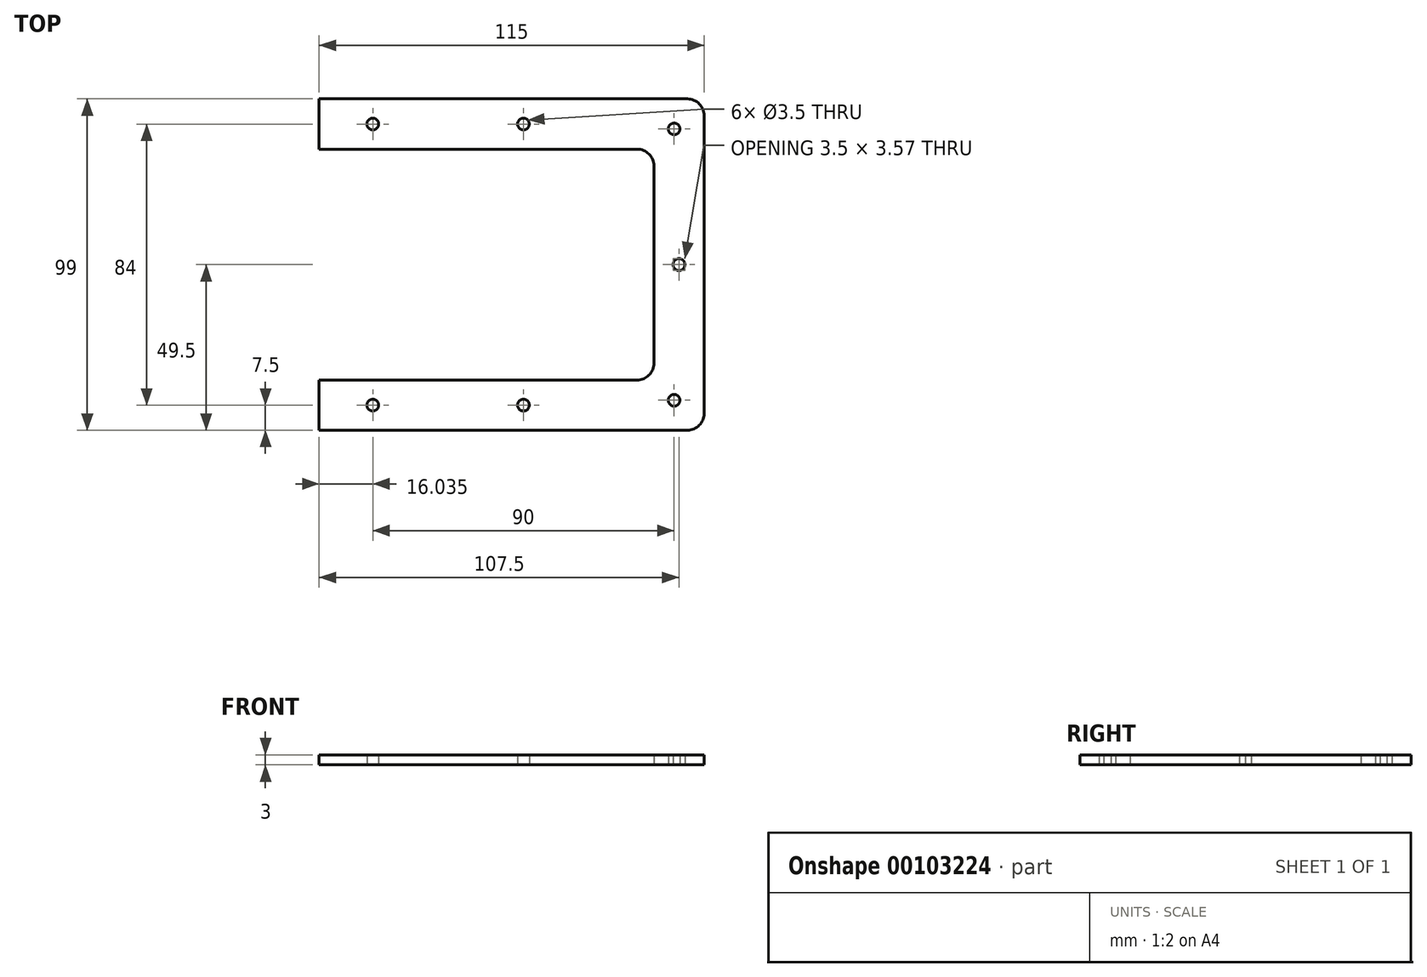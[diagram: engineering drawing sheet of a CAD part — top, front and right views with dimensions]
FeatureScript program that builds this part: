
annotation { "Feature Type Name" : "Feature", "Feature Type Description" : "" }
export const myFeature = defineFeature(function(context is Context, id is Id, definition is map)
    precondition{}
    {
        {
            var Q0;
            Q0=qCreatedBy(makeId("Top.planeOp"),FACE);
            var sketch = newSketch(context, id + "F0", { "sketchPlane" : qUnion([Q0])});
            skLineSegment(sketch, "E0.bottom", {"start": v(95, -34.5) * mm, "end": v(0, -34.5) * mm});
            skLineSegment(sketch, "E0.top", {"start": v(95, 34.5) * mm, "end": v(0, 34.5) * mm});
            skLineSegment(sketch, "E0.left", {"start": v(100, -29.5) * mm, "end": v(100, 29.5) * mm});
            skPoint(sketch, "E0.middle", {"position": v(0, 0) * mm});
            skLineSegment(sketch, "E1.1", {"start": v(110, -49.5) * mm, "end": v(0, -49.5) * mm});
            skLineSegment(sketch, "E1.2", {"start": v(115, -44.5) * mm, "end": v(115, 44.5) * mm});
            skLineSegment(sketch, "E1.3", {"start": v(110, 49.5) * mm, "end": v(0, 49.5) * mm});
            skPoint(sketch, "E2.visualSharp", {"position": v(115, -49.5) * mm});
            skArc(sketch, "E2.filletArc", {"start": v(110, -49.5) * mm, "mid": v(113.54, -48.04) * mm, "end": v(115, -44.5) * mm});
            skPoint(sketch, "E3.visualSharp", {"position": v(115, 49.5) * mm});
            skArc(sketch, "E3.filletArc", {"start": v(115, 44.5) * mm, "mid": v(113.54, 48.04) * mm, "end": v(110, 49.5) * mm});
            skPoint(sketch, "E4.visualSharp", {"position": v(100, 34.5) * mm});
            skArc(sketch, "E4.filletArc", {"start": v(100, 29.5) * mm, "mid": v(98.54, 33.04) * mm, "end": v(95, 34.5) * mm});
            skPoint(sketch, "E5.visualSharp", {"position": v(100, -34.5) * mm});
            skArc(sketch, "E5.filletArc", {"start": v(95, -34.5) * mm, "mid": v(98.54, -33.04) * mm, "end": v(100, -29.5) * mm});
            skLineSegment(sketch, "E6", {"start": v(0, 49.5) * mm, "end": v(0, 34.5) * mm, "construction": true});
            skLineSegment(sketch, "E7", {"start": v(0, 34.5) * mm, "end": v(0, 42) * mm, "construction": true});
            skLineSegment(sketch, "E8", {"start": v(0, 42) * mm, "end": v(102.5, 42) * mm, "construction": true});
            skLineSegment(sketch, "E9", {"start": v(100, 0) * mm, "end": v(115, 0) * mm, "construction": true});
            skLineSegment(sketch, "E10", {"start": v(107.5, 0) * mm, "end": v(107.5, 37) * mm, "construction": true});
            skArc(sketch, "E11.filletArc", {"start": v(107.5, 37) * mm, "mid": v(106.04, 40.54) * mm, "end": v(102.5, 42) * mm, "construction": true});
            skLineSegment(sketch, "E12", {"start": v(98.54, 33.04) * mm, "end": v(113.54, 48.04) * mm, "construction": true});
            skPoint(sketch, "E13", {"position": v(106.04, 40.54) * mm});
            skPoint(sketch, "E14", {"position": v(107.5, 0.04) * mm});
            skPoint(sketch, "E15", {"position": v(61.04, 42) * mm});
            skPoint(sketch, "E16", {"position": v(16.04, 42) * mm});
            skPoint(sketch, "E17.MirrorP", {"position": v(107.5, -0.04) * mm});
            skPoint(sketch, "E18.MirrorP", {"position": v(106.04, -40.54) * mm});
            skPoint(sketch, "E19.MirrorP", {"position": v(61.04, -42) * mm});
            skPoint(sketch, "E20.MirrorP", {"position": v(16.04, -42) * mm});
            skLineSegment(sketch, "E21", {"start": v(0, 49.5) * mm, "end": v(0, 34.5) * mm});
            skLineSegment(sketch, "E22", {"start": v(0, -34.5) * mm, "end": v(0, -49.5) * mm});
            skSolve(sketch);
        }
        {
            var Q0;
            Q0=makeQuery(id+"F0.imprint","IMPRINT",FACE,{"disambiguationData":[TD([[makeQuery(id+"F0.imprint","IMPRINT",EDGE,{"derivedFrom":sQuery(id+"F0.wireOp",EDGE,"E0.bottom")}),1.0]])]});
            extrude(context, id + "F1", {"entities" : qUnion([Q0]), "depth" : 3 * mm});
        }
        {
            var Q0;
            Q0=sQuery(id+"F0.wireOp",VERTEX,"E16");
            var Q1;
            Q1=sQuery(id+"F0.wireOp",VERTEX,"E15");
            var Q2;
            Q2=sQuery(id+"F0.wireOp",VERTEX,"E13");
            var Q3;
            Q3=sQuery(id+"F0.wireOp",VERTEX,"E14");
            var Q4;
            Q4=sQuery(id+"F0.wireOp",VERTEX,"E17.MirrorP");
            var Q5;
            Q5=sQuery(id+"F0.wireOp",VERTEX,"E18.MirrorP");
            var Q6;
            Q6=sQuery(id+"F0.wireOp",VERTEX,"E19.MirrorP");
            var Q7;
            Q7=sQuery(id+"F0.wireOp",VERTEX,"E20.MirrorP");
            var Q8;
            Q8=makeQuery(id+"F1.opExtrude","SWEPT_BODY",BODY,{"disambiguationData":[OSD([sQuery(id+"F0.wireOp",EDGE,"E0.bottom"),sQuery(id+"F0.wireOp",EDGE,"E0.top"),sQuery(id+"F0.wireOp",EDGE,"E0.left"),sQuery(id+"F0.wireOp",EDGE,"E1.1"),sQuery(id+"F0.wireOp",EDGE,"E1.2"),sQuery(id+"F0.wireOp",EDGE,"E1.3"),sQuery(id+"F0.wireOp",EDGE,"E2.filletArc"),sQuery(id+"F0.wireOp",EDGE,"E3.filletArc"),sQuery(id+"F0.wireOp",EDGE,"E4.filletArc"),sQuery(id+"F0.wireOp",EDGE,"E5.filletArc"),sQuery(id+"F0.wireOp",EDGE,"E21"),sQuery(id+"F0.wireOp",EDGE,"E22")])]});
            hole(context, id + "F2", {"style" : HoleStyle.SIMPLE, "endStyle" : HoleEndStyle.BLIND, "oppositeDirection" : true, "holeDiameter" : 3.5 * mm, "holeDepth" : 5 * mm, "locations" : qUnion([Q0, Q1, Q2, Q3, Q4, Q5, Q6, Q7]), "scope" : qUnion([Q8])});
        }
    });
